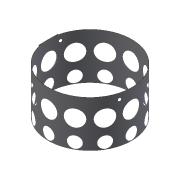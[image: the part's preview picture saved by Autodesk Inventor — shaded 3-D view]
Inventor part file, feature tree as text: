
AUTODESK INVENTOR PART (.ipt)
format: ipt  version: 2016 (Build 200138000, 138)  size: 342,528 bytes
history: native  units: in
note: dims shown in document units (in); Inventor stores cm internally (conversion verified against a paired STEP export)
features: sketch x8, plane x4, extrude x3, other x1, hole x1, pattern_circular x1
ambient origin geometry x8: Origin, YZ Plane, XZ Plane, XY Plane, X Axis, Y Axis, Z Axis, Center Point
bodies: Solid1 (feature_tree)
feature tree (18):
  extrude  "tube"  Depth=10.0in TaperAngle=0.0deg
  sketch  "Sketch2"  dims[d45=0.0773in d97=165.0deg]
  other  "Work Point1"
  plane  "Work Plane1"
  sketch  "Sketch7"  dims[d112=18.0in d114=0.5906in]
  plane  "Work Plane2"
  sketch  "Sketch15"  dims[d115=1.2598in]
  plane  "Work Plane5"
  sketch  "Sketch17"  dims[d116=0.5906in d117=0.75in d118=0.375in d119=0.25in d120=0.5635in d121=1.0in d122=0.8108in d124=0.0394in d125=0.0in]
  plane  "Work Plane7"
  hole  "rebar"  [1 undecoded]
  extrude  "fakeExtrude"  Depth=0.5906in
  extrude  "sleeveSupportHoles"  Depth=0.0394in TaperAngle=0.0deg
  pattern_circular  "Circular Pattern4"  Count=15  [1 undecoded]
  sketch  "Sketch1"  dims[d2=0.06in d3=10.0in d4=0.0in]
  sketch  "Sketch22"  dims[d126=3.5827in]
  sketch  "Sketch23"  dims[d127=2.5197in]
  sketch  "Sketch24"  dims[d128=1.3976in d129=5.9055in d130=2.0in d131=0.0in d132=4.7244in d133=360.0deg]
note: 2 required parameter values undecoded (feature->parameter linkage not recoverable at this tier; creation-order binding heuristic only, values carry confidence <= 0.55)
